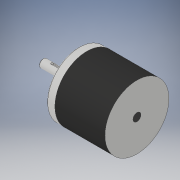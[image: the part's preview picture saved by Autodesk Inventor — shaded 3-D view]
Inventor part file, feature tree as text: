
AUTODESK INVENTOR PART (.ipt)
format: ipt  version: 2019 (Build 230136000, 136)  size: 157,184 bytes
history: native  units: in
note: dims shown in document units (in); Inventor stores cm internally (conversion verified against a paired STEP export)
features: delete_face x2, chamfer x1, extrude x1, sketch x1
ambient origin geometry x8: Origin, YZ Plane, XZ Plane, XY Plane, X Axis, Y Axis, Z Axis, Center Point
bodies: Solid1 (feature_tree)
feature tree (5):
  chamfer  "Chamfer3"  Distance=2.212in
  extrude  "Extrusion1"  [1 undecoded]
  delete_face  "Delete Face1"
  delete_face  "Delete Face2"
  sketch  "Sketch1"
note: 1 required parameter value undecoded (feature->parameter linkage not recoverable at this tier; creation-order binding heuristic only, values carry confidence <= 0.55)
